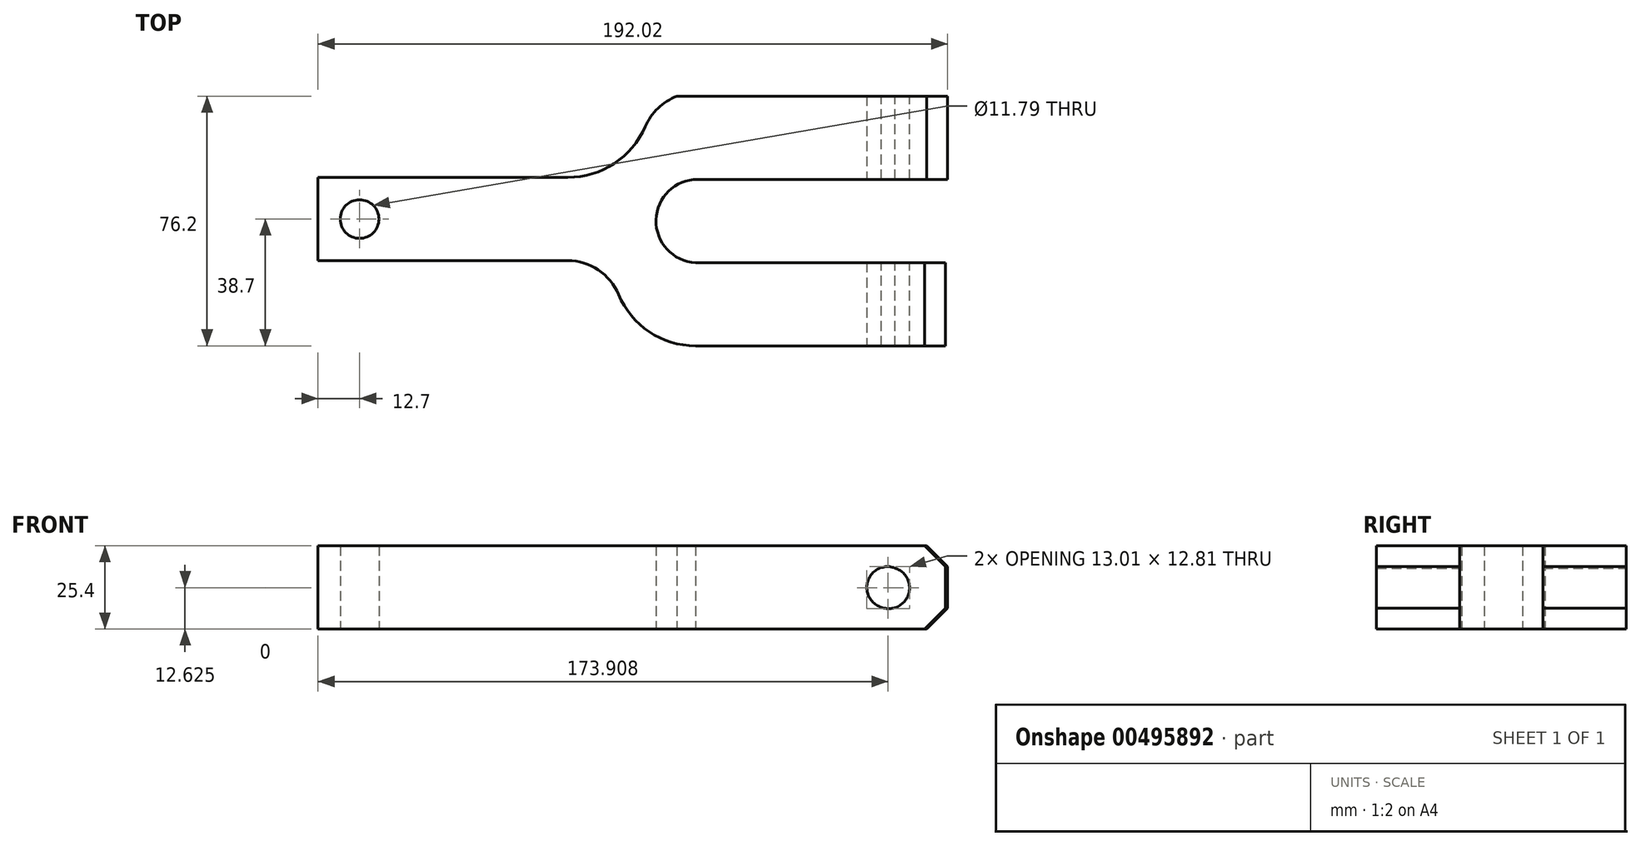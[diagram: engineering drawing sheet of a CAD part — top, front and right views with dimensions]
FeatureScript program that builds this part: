
annotation { "Feature Type Name" : "Feature", "Feature Type Description" : "" }
export const myFeature = defineFeature(function(context is Context, id is Id, definition is map)
    precondition{}
    {
        {
            var Q0;
            Q0=qCreatedBy(makeId("Top.planeOp"),FACE);
            var sketch = newSketch(context, id + "F0", { "sketchPlane" : qUnion([Q0])});
            skLineSegment(sketch, "E0", {"start": v(0, 12.7) * mm, "end": v(-76.2, 12.7) * mm});
            skLineSegment(sketch, "E1", {"start": v(-76.2, 12.7) * mm, "end": v(-76.2, -12.7) * mm});
            skLineSegment(sketch, "E2", {"start": v(-76.2, -12.7) * mm, "end": v(0, -12.7) * mm});
            skArc(sketch, "E3", {"start": v(0, 12.7) * mm, "mid": v(14.14, 16.92) * mm, "end": v(23.64, 28.21) * mm});
            skArc(sketch, "E4", {"start": v(23.64, 28.21) * mm, "mid": v(27.52, 33.82) * mm, "end": v(33.26, 37.5) * mm});
            skLineSegment(sketch, "E5", {"start": v(33.26, 37.5) * mm, "end": v(115.82, 37.5) * mm});
            skLineSegment(sketch, "E6", {"start": v(115.82, 37.5) * mm, "end": v(115.82, 12.1) * mm});
            skLineSegment(sketch, "E7", {"start": v(115.82, 12.1) * mm, "end": v(39.62, 12.1) * mm});
            skArc(sketch, "E8", {"start": v(0, -12.7) * mm, "mid": v(9.3, -15.52) * mm, "end": v(15.48, -23.04) * mm});
            skArc(sketch, "E9", {"start": v(15.48, -23.04) * mm, "mid": v(24.84, -34.42) * mm, "end": v(38.94, -38.7) * mm});
            skLineSegment(sketch, "E10", {"start": v(38.94, -38.7) * mm, "end": v(115.14, -38.7) * mm});
            skLineSegment(sketch, "E11", {"start": v(38.94, -13.3) * mm, "end": v(115.14, -13.3) * mm});
            skLineSegment(sketch, "E12", {"start": v(115.14, -13.3) * mm, "end": v(115.14, -38.7) * mm});
            skCircle(sketch, "E13", {"center": v(-63.5, 0) * mm, "radius": 5.9 * mm});
            skPoint(sketch, "E13.first.point", {"position": v(-57.6, 0) * mm});
            skPoint(sketch, "E13.first.point.positionSnap0", {"position": v(-76.2, 0) * mm});
            skPoint(sketch, "E13.second.point", {"position": v(-57.6, 0) * mm});
            skPoint(sketch, "E13.second.point.positionSnap0", {"position": v(-76.2, 0) * mm});
            skPoint(sketch, "E13.third.point", {"position": v(-68.12, 3.66) * mm});
            skArc(sketch, "E14", {"start": v(39.62, 12.1) * mm, "mid": v(26.92, -0.27) * mm, "end": v(38.94, -13.3) * mm});
            skSolve(sketch);
        }
        {
            var Q0;
            Q0 = qSketchRegion(id + "F0", true);
            extrude(context, id + "F1", {"entities" : qUnion([Q0]), "depth" : 25.4 * mm});
        }
        {
            var Q0;
            Q0=makeQuery(id+"F1.opExtrude","SWEPT_FACE",FACE,{"disambiguationData":[OSD([sQuery(id+"F0.wireOp",EDGE,"E10")])]});
            var sketch = newSketch(context, id + "F2", { "sketchPlane" : qUnion([Q0])});
            skCircle(sketch, "E15", {"center": v(97.54, 12.68) * mm, "radius": 7.38 * mm});
            skPoint(sketch, "E15.first.point", {"position": v(91.5, 16.9) * mm});
            skPoint(sketch, "E15.second.point", {"position": v(103.83, 8.83) * mm});
            skPoint(sketch, "E15.third.point", {"position": v(90.22, 11.8) * mm});
            skSolve(sketch);
        }
        {
            var Q0;
            Q0=makeQuery(id+"F1.opExtrude","SWEPT_FACE",FACE,{"disambiguationData":[OSD([sQuery(id+"F0.wireOp",EDGE,"E5")])]});
            var sketch = newSketch(context, id + "F3", { "sketchPlane" : qUnion([Q0])});
            skCircle(sketch, "E16", {"center": v(-97.87, 12.57) * mm, "radius": 8.01 * mm});
            skPoint(sketch, "E16.first.point", {"position": v(-104.1, 7.52) * mm});
            skPoint(sketch, "E16.second.point", {"position": v(-91.32, 17.18) * mm});
            skPoint(sketch, "E16.third.point", {"position": v(-89.9, 13.24) * mm});
            skSolve(sketch);
        }
        {
            var Q0;
            Q0=sQuery(id+"F2.wireOp",VERTEX,"E15.center");
            var Q1;
            Q1=sQuery(id+"F3.wireOp",VERTEX,"E16.center");
            var Q2;
            Q2=makeQuery(id+"F1.opExtrude","SWEPT_BODY",BODY,{"disambiguationData":[OSD([sQuery(id+"F0.wireOp",EDGE,"E0"),sQuery(id+"F0.wireOp",EDGE,"E1"),sQuery(id+"F0.wireOp",EDGE,"E2"),sQuery(id+"F0.wireOp",EDGE,"E3"),sQuery(id+"F0.wireOp",EDGE,"E4"),sQuery(id+"F0.wireOp",EDGE,"E5"),sQuery(id+"F0.wireOp",EDGE,"E6"),sQuery(id+"F0.wireOp",EDGE,"E7"),sQuery(id+"F0.wireOp",EDGE,"E8"),sQuery(id+"F0.wireOp",EDGE,"E9"),sQuery(id+"F0.wireOp",EDGE,"E10"),sQuery(id+"F0.wireOp",EDGE,"E11"),sQuery(id+"F0.wireOp",EDGE,"E12"),sQuery(id+"F0.wireOp",EDGE,"E13"),sQuery(id+"F0.wireOp",EDGE,"E14")])]});
            hole(context, id + "F4", {"style" : HoleStyle.SIMPLE, "endStyle" : HoleEndStyle.THROUGH, "holeDiameter" : 12.7 * mm, "isTappedThrough" : true, "tappedDepth" : 12.7 * mm, "tapClearance" : 3, "locations" : qUnion([Q0, Q1]), "scope" : qUnion([Q2])});
        }
        {
            var Q0;
            Q0=makeQuery(id+"F1.opExtrude","CAP_EDGE",EDGE,{"disambiguationData":[OSD([sQuery(id+"F0.wireOp",EDGE,"E12")])],"isStart":false});
            var Q1;
            Q1=makeQuery(id+"F1.opExtrude","CAP_EDGE",EDGE,{"disambiguationData":[OSD([sQuery(id+"F0.wireOp",EDGE,"E12")])],"isStart":true});
            var Q2;
            Q2=makeQuery(id+"F1.opExtrude","CAP_EDGE",EDGE,{"disambiguationData":[OSD([sQuery(id+"F0.wireOp",EDGE,"E6")])],"isStart":false});
            var Q3;
            Q3=makeQuery(id+"F1.opExtrude","CAP_EDGE",EDGE,{"disambiguationData":[OSD([sQuery(id+"F0.wireOp",EDGE,"E6")])],"isStart":true});
            chamfer(context, id + "F5", {"entities" : qUnion([Q0, Q1, Q2, Q3]), "width" : 6.35 * mm, "tangentPropagation" : true});
        }
    });
